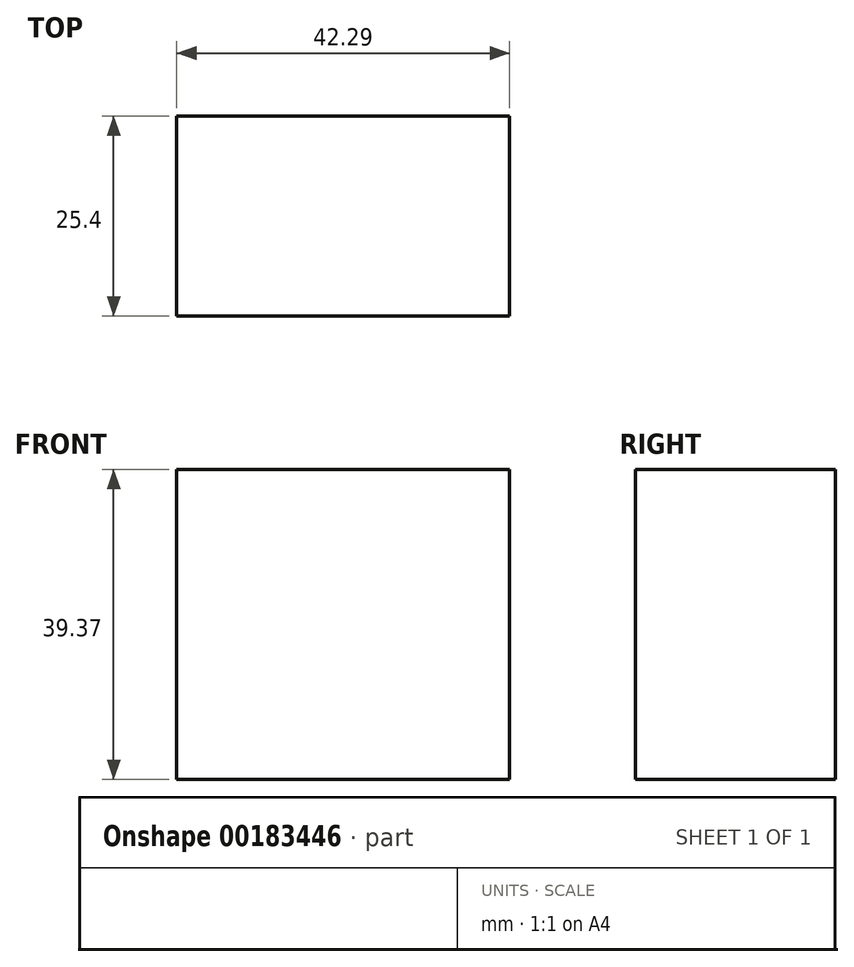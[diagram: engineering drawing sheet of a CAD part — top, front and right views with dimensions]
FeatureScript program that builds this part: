
annotation { "Feature Type Name" : "Feature", "Feature Type Description" : "" }
export const myFeature = defineFeature(function(context is Context, id is Id, definition is map)
    precondition{}
    {
        {
            var Q0;
            Q0=qCreatedBy(makeId("Front.planeOp"),FACE);
            var sketch = newSketch(context, id + "F0", { "sketchPlane" : qUnion([Q0])});
            skLineSegment(sketch, "E0.bottom", {"start": v(0, 0) * mm, "end": v(42.29, 0) * mm});
            skLineSegment(sketch, "E0.top", {"start": v(0, 39.37) * mm, "end": v(42.29, 39.37) * mm});
            skLineSegment(sketch, "E0.left", {"start": v(0, 0) * mm, "end": v(0, 39.37) * mm});
            skLineSegment(sketch, "E0.right", {"start": v(42.29, 0) * mm, "end": v(42.29, 39.37) * mm});
            skSolve(sketch);
        }
        {
            var Q0;
            Q0 = qSketchRegion(id + "F0", true);
            extrude(context, id + "F1", {"entities" : qUnion([Q0]), "depth" : 25.4 * mm});
        }
    });
